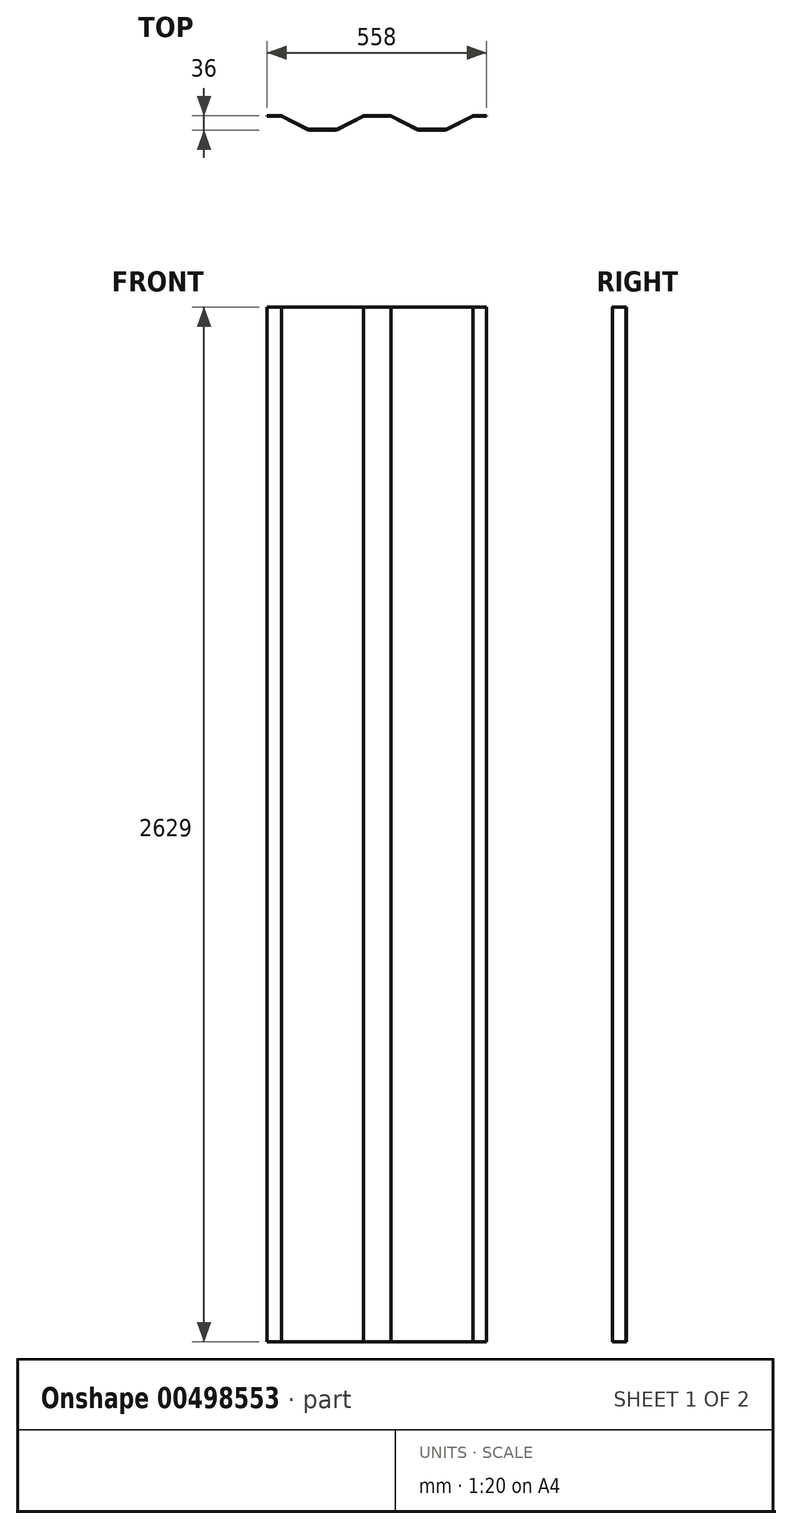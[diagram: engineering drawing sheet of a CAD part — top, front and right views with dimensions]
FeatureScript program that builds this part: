
annotation { "Feature Type Name" : "Feature", "Feature Type Description" : "" }
export const myFeature = defineFeature(function(context is Context, id is Id, definition is map)
    precondition{}
    {
        {
            var Q0;
            Q0=qCreatedBy(makeId("Top.planeOp"),FACE);
            var sketch = newSketch(context, id + "F0", { "sketchPlane" : qUnion([Q0])});
            skLineSegment(sketch, "E0", {"start": v(0, 0) * mm, "end": v(1116, 0) * mm});
            skLineSegment(sketch, "E1", {"start": v(0, 15.22) * mm, "end": v(37, 15.22) * mm});
            skLineSegment(sketch, "E2", {"start": v(37, 15.22) * mm, "end": v(105, 15.22) * mm});
            skLineSegment(sketch, "E3", {"start": v(105, 15.22) * mm, "end": v(177, 15.22) * mm});
            skLineSegment(sketch, "E4", {"start": v(177, 15.22) * mm, "end": v(245, 15.22) * mm});
            skLineSegment(sketch, "E5", {"start": v(245, 15.22) * mm, "end": v(315, 15.22) * mm});
            skLineSegment(sketch, "E6", {"start": v(315, 15.22) * mm, "end": v(383, 15.22) * mm});
            skLineSegment(sketch, "E7", {"start": v(383, 15.22) * mm, "end": v(455, 15.22) * mm});
            skLineSegment(sketch, "E8", {"start": v(455, 15.22) * mm, "end": v(523, 15.22) * mm});
            skLineSegment(sketch, "E9", {"start": v(523, 15.22) * mm, "end": v(593, 15.22) * mm});
            skLineSegment(sketch, "E10", {"start": v(593, 15.22) * mm, "end": v(661, 15.22) * mm});
            skLineSegment(sketch, "E11", {"start": v(661, 15.22) * mm, "end": v(733, 15.22) * mm});
            skLineSegment(sketch, "E12", {"start": v(733, 15.22) * mm, "end": v(801, 15.22) * mm});
            skLineSegment(sketch, "E13", {"start": v(801, 15.22) * mm, "end": v(871, 15.22) * mm});
            skLineSegment(sketch, "E14", {"start": v(871, 15.22) * mm, "end": v(939, 15.22) * mm});
            skLineSegment(sketch, "E15", {"start": v(939, 15.22) * mm, "end": v(1011, 15.22) * mm});
            skLineSegment(sketch, "E16", {"start": v(1011, 15.22) * mm, "end": v(1079, 15.22) * mm});
            skLineSegment(sketch, "E17", {"start": v(1079, 15.22) * mm, "end": v(1116, 15.22) * mm});
            skLineSegment(sketch, "E18", {"start": v(1116, 15.22) * mm, "end": v(1116, 51.22) * mm});
            skLineSegment(sketch, "E19", {"start": v(1124.7, 15.22) * mm, "end": v(1124.7, 16.82) * mm});
            skLineSegment(sketch, "E20", {"start": v(1116, 51.22) * mm, "end": v(1080.2, 51.22) * mm});
            skLineSegment(sketch, "E21", {"start": v(1077.94, 50.68) * mm, "end": v(1012.06, 17.36) * mm});
            skLineSegment(sketch, "E22", {"start": v(1009.8, 16.82) * mm, "end": v(940.2, 16.82) * mm});
            skLineSegment(sketch, "E23", {"start": v(937.94, 17.36) * mm, "end": v(872.06, 50.68) * mm});
            skLineSegment(sketch, "E24", {"start": v(869.8, 51.22) * mm, "end": v(802.2, 51.22) * mm});
            skLineSegment(sketch, "E25", {"start": v(799.94, 50.68) * mm, "end": v(734.06, 17.36) * mm});
            skLineSegment(sketch, "E26", {"start": v(731.8, 16.82) * mm, "end": v(662.2, 16.82) * mm});
            skLineSegment(sketch, "E27", {"start": v(659.94, 17.36) * mm, "end": v(594.06, 50.68) * mm});
            skLineSegment(sketch, "E28", {"start": v(591.8, 51.22) * mm, "end": v(524.2, 51.22) * mm});
            skLineSegment(sketch, "E29", {"start": v(456.06, 17.36) * mm, "end": v(521.94, 50.68) * mm});
            skLineSegment(sketch, "E30", {"start": v(453.8, 16.82) * mm, "end": v(384.2, 16.82) * mm});
            skLineSegment(sketch, "E31", {"start": v(381.94, 17.36) * mm, "end": v(316.06, 50.68) * mm});
            skLineSegment(sketch, "E32", {"start": v(313.8, 51.22) * mm, "end": v(246.2, 51.22) * mm});
            skLineSegment(sketch, "E33", {"start": v(243.94, 50.68) * mm, "end": v(178.06, 17.36) * mm});
            skLineSegment(sketch, "E34", {"start": v(175.8, 16.82) * mm, "end": v(106.2, 16.82) * mm});
            skLineSegment(sketch, "E35", {"start": v(103.94, 17.36) * mm, "end": v(38.06, 50.68) * mm});
            skLineSegment(sketch, "E36", {"start": v(35.8, 51.22) * mm, "end": v(0, 51.22) * mm});
            skPoint(sketch, "E37.visualSharp", {"position": v(1079, 51.22) * mm});
            skArc(sketch, "E37.filletArc", {"start": v(1080.2, 51.22) * mm, "mid": v(1079.03, 51.09) * mm, "end": v(1077.94, 50.68) * mm});
            skPoint(sketch, "E38.visualSharp", {"position": v(1011, 16.82) * mm});
            skArc(sketch, "E38.filletArc", {"start": v(1009.8, 16.82) * mm, "mid": v(1010.97, 16.96) * mm, "end": v(1012.06, 17.36) * mm});
            skPoint(sketch, "E39.visualSharp", {"position": v(939, 16.82) * mm});
            skArc(sketch, "E39.filletArc", {"start": v(937.94, 17.36) * mm, "mid": v(939.03, 16.96) * mm, "end": v(940.2, 16.82) * mm});
            skPoint(sketch, "E40.visualSharp", {"position": v(871, 51.22) * mm});
            skArc(sketch, "E40.filletArc", {"start": v(872.06, 50.68) * mm, "mid": v(870.97, 51.09) * mm, "end": v(869.8, 51.22) * mm});
            skPoint(sketch, "E41.visualSharp", {"position": v(801, 51.22) * mm});
            skArc(sketch, "E41.filletArc", {"start": v(802.2, 51.22) * mm, "mid": v(801.03, 51.09) * mm, "end": v(799.94, 50.68) * mm});
            skPoint(sketch, "E42.visualSharp", {"position": v(733, 16.82) * mm});
            skArc(sketch, "E42.filletArc", {"start": v(731.8, 16.82) * mm, "mid": v(732.97, 16.96) * mm, "end": v(734.06, 17.36) * mm});
            skPoint(sketch, "E43.visualSharp", {"position": v(661, 16.82) * mm});
            skArc(sketch, "E43.filletArc", {"start": v(659.94, 17.36) * mm, "mid": v(661.03, 16.96) * mm, "end": v(662.2, 16.82) * mm});
            skPoint(sketch, "E44.visualSharp", {"position": v(593, 51.22) * mm});
            skArc(sketch, "E44.filletArc", {"start": v(594.06, 50.68) * mm, "mid": v(592.97, 51.09) * mm, "end": v(591.8, 51.22) * mm});
            skPoint(sketch, "E45.visualSharp", {"position": v(523, 51.22) * mm});
            skArc(sketch, "E45.filletArc", {"start": v(524.2, 51.22) * mm, "mid": v(523.03, 51.09) * mm, "end": v(521.94, 50.68) * mm});
            skPoint(sketch, "E46.visualSharp", {"position": v(455, 16.82) * mm});
            skArc(sketch, "E46.filletArc", {"start": v(453.8, 16.82) * mm, "mid": v(454.97, 16.96) * mm, "end": v(456.06, 17.36) * mm});
            skPoint(sketch, "E47.visualSharp", {"position": v(383, 16.82) * mm});
            skArc(sketch, "E47.filletArc", {"start": v(381.94, 17.36) * mm, "mid": v(383.03, 16.96) * mm, "end": v(384.2, 16.82) * mm});
            skPoint(sketch, "E48.visualSharp", {"position": v(315, 51.22) * mm});
            skArc(sketch, "E48.filletArc", {"start": v(316.06, 50.68) * mm, "mid": v(314.97, 51.09) * mm, "end": v(313.8, 51.22) * mm});
            skPoint(sketch, "E49.visualSharp", {"position": v(245, 51.22) * mm});
            skArc(sketch, "E49.filletArc", {"start": v(246.2, 51.22) * mm, "mid": v(245.03, 51.09) * mm, "end": v(243.94, 50.68) * mm});
            skPoint(sketch, "E50.visualSharp", {"position": v(177, 16.82) * mm});
            skArc(sketch, "E50.filletArc", {"start": v(175.8, 16.82) * mm, "mid": v(176.97, 16.96) * mm, "end": v(178.06, 17.36) * mm});
            skPoint(sketch, "E51.visualSharp", {"position": v(37, 51.22) * mm});
            skArc(sketch, "E51.filletArc", {"start": v(38.06, 50.68) * mm, "mid": v(36.97, 51.09) * mm, "end": v(35.8, 51.22) * mm});
            skPoint(sketch, "E52.visualSharp", {"position": v(105, 16.82) * mm});
            skArc(sketch, "E52.filletArc", {"start": v(103.94, 17.36) * mm, "mid": v(105.03, 16.96) * mm, "end": v(106.2, 16.82) * mm});
            skLineSegment(sketch, "E53.0", {"start": v(36.62, 49.62) * mm, "end": v(0, 49.62) * mm});
            skLineSegment(sketch, "E53.1", {"start": v(103.21, 15.93) * mm, "end": v(36.62, 49.62) * mm});
            skArc(sketch, "E53.2", {"start": v(103.21, 15.93) * mm, "mid": v(104.66, 15.4) * mm, "end": v(106.2, 15.22) * mm});
            skLineSegment(sketch, "E53.3", {"start": v(731.8, 15.22) * mm, "end": v(662.2, 15.22) * mm});
            skArc(sketch, "E53.4", {"start": v(731.8, 15.22) * mm, "mid": v(733.34, 15.4) * mm, "end": v(734.79, 15.93) * mm});
            skLineSegment(sketch, "E53.5", {"start": v(801.38, 49.62) * mm, "end": v(734.79, 15.93) * mm});
            skLineSegment(sketch, "E53.6", {"start": v(870.62, 49.62) * mm, "end": v(801.38, 49.62) * mm});
            skLineSegment(sketch, "E53.7", {"start": v(937.21, 15.93) * mm, "end": v(870.62, 49.62) * mm});
            skArc(sketch, "E53.8", {"start": v(937.21, 15.93) * mm, "mid": v(938.66, 15.4) * mm, "end": v(940.2, 15.22) * mm});
            skLineSegment(sketch, "E53.9", {"start": v(1116, 49.62) * mm, "end": v(1079.38, 49.62) * mm});
            skLineSegment(sketch, "E53.10", {"start": v(1079.38, 49.62) * mm, "end": v(1012.79, 15.93) * mm});
            skArc(sketch, "E53.11", {"start": v(1009.8, 15.22) * mm, "mid": v(1011.34, 15.4) * mm, "end": v(1012.79, 15.93) * mm});
            skLineSegment(sketch, "E53.12", {"start": v(1009.8, 15.22) * mm, "end": v(940.2, 15.22) * mm});
            skArc(sketch, "E53.13", {"start": v(659.21, 15.93) * mm, "mid": v(660.66, 15.4) * mm, "end": v(662.2, 15.22) * mm});
            skLineSegment(sketch, "E53.14", {"start": v(659.21, 15.93) * mm, "end": v(592.62, 49.62) * mm});
            skLineSegment(sketch, "E53.15", {"start": v(592.62, 49.62) * mm, "end": v(523.38, 49.62) * mm});
            skLineSegment(sketch, "E53.16", {"start": v(456.79, 15.93) * mm, "end": v(523.38, 49.62) * mm});
            skArc(sketch, "E53.17", {"start": v(453.8, 15.22) * mm, "mid": v(455.34, 15.4) * mm, "end": v(456.79, 15.93) * mm});
            skLineSegment(sketch, "E53.18", {"start": v(453.8, 15.22) * mm, "end": v(384.2, 15.22) * mm});
            skArc(sketch, "E53.19", {"start": v(381.21, 15.93) * mm, "mid": v(382.66, 15.4) * mm, "end": v(384.2, 15.22) * mm});
            skLineSegment(sketch, "E53.20", {"start": v(381.21, 15.93) * mm, "end": v(314.62, 49.62) * mm});
            skLineSegment(sketch, "E53.21", {"start": v(314.62, 49.62) * mm, "end": v(245.38, 49.62) * mm});
            skLineSegment(sketch, "E53.22", {"start": v(245.38, 49.62) * mm, "end": v(178.79, 15.93) * mm});
            skArc(sketch, "E53.23", {"start": v(175.8, 15.22) * mm, "mid": v(177.34, 15.4) * mm, "end": v(178.79, 15.93) * mm});
            skLineSegment(sketch, "E53.24", {"start": v(175.8, 15.22) * mm, "end": v(106.2, 15.22) * mm});
            skLineSegment(sketch, "E54", {"start": v(0, 51.22) * mm, "end": v(0, 49.62) * mm});
            skSolve(sketch);
        }
        {
            var Q0;
            {var subQ1=sQuery(id+"F0.wireOp",EDGE,"E20");Q0=makeQuery(id+"F0.imprint","IMPRINT",FACE,{"disambiguationData":[TD([[makeQuery(id+"F0.imprint","IMPRINT",EDGE,{"derivedFrom":subQ1}),1.0]])]});}
            extrude(context, id + "F1", {"entities" : qUnion([Q0]), "depth" : 2629 * mm});
        }
        {
            var Q0;
            Q0=makeQuery(id+"F1.opExtrude","SWEPT_FACE",FACE,{"disambiguationData":[OSD([sQuery(id+"F0.wireOp",EDGE,"E28")])]});
            var sketch = newSketch(context, id + "F2", { "sketchPlane" : qUnion([Q0])});
            skLineSegment(sketch, "E55.bottom", {"start": v(-558, 2629) * mm, "end": v(-1279.21, 2629) * mm});
            skLineSegment(sketch, "E55.top", {"start": v(-558, -48.76) * mm, "end": v(-1279.21, -48.76) * mm});
            skLineSegment(sketch, "E55.left", {"start": v(-558, 2629) * mm, "end": v(-558, -48.76) * mm});
            skLineSegment(sketch, "E55.right", {"start": v(-1279.21, 2629) * mm, "end": v(-1279.21, -48.76) * mm});
            skSolve(sketch);
        }
        {
            var Q0;
            Q0 = qSketchRegion(id + "F2", true);
            extrude(context, id + "F3", {"entities" : qUnion([Q0]), "operationType" : NewBodyOperationType.REMOVE, "endBound" : BoundingType.THROUGH_ALL, "oppositeDirection" : true, "depth" : 25 * mm});
        }
    });
